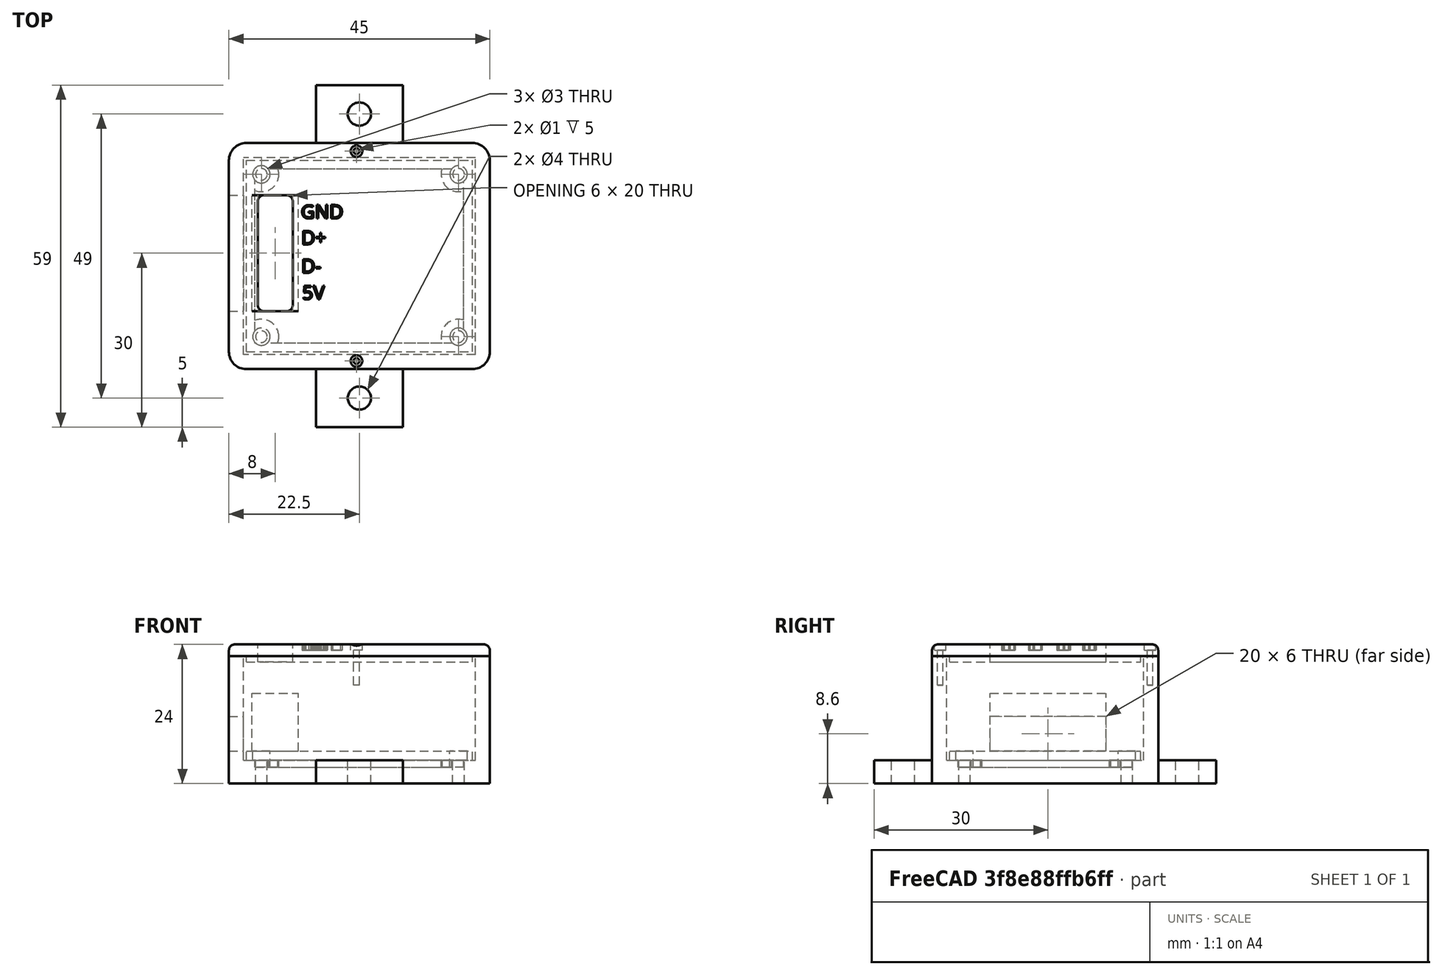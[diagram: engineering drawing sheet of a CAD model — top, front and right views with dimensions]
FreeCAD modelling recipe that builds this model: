
FCSTD DOCUMENT  (FreeCAD 0.17R13522 (Git))
Label: Caja Bridge TCP-RTU V2
License: All rights reserved
LicenseURL: http://en.wikipedia.org/wiki/All_rights_reserved
objects: Part::Cylinder×20, Part::Box×12, Part::MultiFuse×12, Part::Cut×11, Part::Fillet×4, Part::Part2DObjectPython×4, Part::Extrusion×4
note: 67 computed .brp shape members not serialized (recipe doc carries the construction recipe); baked Part::Feature solids carry a one-line shape summary decoded from their .brp

FEATURE [Part::Box] Box  label="Cubo"
  AttacherType = Attacher::AttachEngine3D
  Height = 1.6
  Length = 39
  Placement = pos=(0,12,0) rot=(0,0,1;0rad)
  Width = 33
FEATURE [Part::Cylinder] Cylinder  label="Cilindro"
  Angle = 360
  AttacherType = Attacher::AttachEngine3D
  Height = 10
  Placement = pos=(2.6,14.6,-5) rot=(0,0,1;0rad)
  Radius = 1.5
FEATURE [Part::Cylinder] Cylinder001  label="Cilindro001"
  Angle = 360
  AttacherType = Attacher::AttachEngine3D
  Height = 10
  Placement = pos=(36.6,14.6,-5) rot=(0,0,1;0rad)
  Radius = 1.5
FEATURE [Part::Cylinder] Cylinder002  label="Cilindro002"
  Angle = 360
  AttacherType = Attacher::AttachEngine3D
  Height = 10
  Placement = pos=(36.6,42.6,-5) rot=(0,0,1;0rad)
  Radius = 1.5
FEATURE [Part::Cylinder] Cylinder003  label="Cilindro003"
  Angle = 360
  AttacherType = Attacher::AttachEngine3D
  Height = 10
  Placement = pos=(2.6,42.6,-5) rot=(0,0,1;0rad)
  Radius = 1.5
FEATURE [Part::Box] Box001  label="Cubo001"
  AttacherType = Attacher::AttachEngine3D
  Height = 10
  Length = 8
  Placement = pos=(1,19,1.6) rot=(0,0,1;0rad)
  Width = 20
FEATURE [Part::Box] Box002  label="Cubo002"
  AttacherType = Attacher::AttachEngine3D
  Height = 20
  Length = 40
  Placement = pos=(-0.5,11.5,0) rot=(0,0,1;0rad)
  Width = 34
FEATURE [Part::Box] Box003  label="Cubo003"
  AttacherType = Attacher::AttachEngine3D
  Height = 22
  Length = 45
  Placement = pos=(-3,9,-4) rot=(0,0,1;0rad)
  Width = 39
FEATURE [Part::Box] Box004  label="Cubo004"
  AttacherType = Attacher::AttachEngine3D
  Height = 1.5
  Length = 36
  Placement = pos=(1.5,13.5,-1.2) rot=(0,0,1;0rad)
  Width = 30
FEATURE [Part::MultiFuse] Fusion
  Refine = true
  Shapes = -> [Box,Box004]
FEATURE [Part::MultiFuse] Fusion001
  Refine = true
  Shapes = -> [Fusion,Box001]
FEATURE [Part::MultiFuse] Fusion002
  Refine = true
  Shapes = -> [Cylinder,Cylinder003,Cylinder002,Cylinder001]
FEATURE [Part::Cut] Cut  label="Electronica V2"
  Base = -> Fusion001
  Refine = true
  Tool = -> Fusion002
FEATURE [Part::Box] Box005  label="Cubo005"
  AttacherType = Attacher::AttachEngine3D
  Height = 1.5
  Length = 36
  Placement = pos=(1.5,13.5,-1.2) rot=(0,0,1;0rad)
  Width = 30
FEATURE [Part::Box] Box006  label="Cubo006"
  AttacherType = Attacher::AttachEngine3D
  Height = 6
  Length = 22
  Placement = pos=(-10,19,1.6) rot=(0,0,1;0rad)
  Width = 20
FEATURE [Part::Box] Box007  label="Cubo007"
  AttacherType = Attacher::AttachEngine3D
  Height = 2
  Length = 45
  Placement = pos=(-3,9,18) rot=(0,0,1;0rad)
  Width = 39
FEATURE [Part::Box] Box008  label="Cubo008"
  AttacherType = Attacher::AttachEngine3D
  Height = 3
  Length = 39
  Placement = pos=(0,12,17) rot=(0,0,1;0rad)
  Width = 33
FEATURE [Part::Cylinder] Cylinder004  label="Cilindro004"
  Angle = 360
  AttacherType = Attacher::AttachEngine3D
  Height = 10
  Placement = pos=(2.6,14.6,-5) rot=(0,0,1;0rad)
  Radius = 1
FEATURE [Part::Cylinder] Cylinder005  label="Cilindro005"
  Angle = 360
  AttacherType = Attacher::AttachEngine3D
  Height = 10
  Placement = pos=(36.6,14.6,-5) rot=(0,0,1;0rad)
  Radius = 1
FEATURE [Part::Cylinder] Cylinder006  label="Cilindro006"
  Angle = 360
  AttacherType = Attacher::AttachEngine3D
  Height = 10
  Placement = pos=(36.6,42.6,-5) rot=(0,0,1;0rad)
  Radius = 1
FEATURE [Part::Cylinder] Cylinder007  label="Cilindro007"
  Angle = 360
  AttacherType = Attacher::AttachEngine3D
  Height = 10
  Placement = pos=(2.6,42.6,-5) rot=(0,0,1;0rad)
  Radius = 1
FEATURE [Part::Cylinder] Cylinder008  label="Cilindro008"
  Angle = 360
  AttacherType = Attacher::AttachEngine3D
  Height = 3
  Placement = pos=(2.6,42.6,-3) rot=(0,0,1;0rad)
  Radius = 3
FEATURE [Part::Cylinder] Cylinder009  label="Cilindro009"
  Angle = 360
  AttacherType = Attacher::AttachEngine3D
  Height = 3
  Placement = pos=(36.6,14.6,-3) rot=(0,0,1;0rad)
  Radius = 3
FEATURE [Part::Cylinder] Cylinder010  label="Cilindro010"
  Angle = 360
  AttacherType = Attacher::AttachEngine3D
  Height = 3
  Placement = pos=(2.6,14.6,-3) rot=(0,0,1;0rad)
  Radius = 3
FEATURE [Part::Cylinder] Cylinder011  label="Cilindro011"
  Angle = 360
  AttacherType = Attacher::AttachEngine3D
  Height = 3
  Placement = pos=(36.6,42.6,-3) rot=(0,0,1;0rad)
  Radius = 3
FEATURE [Part::MultiFuse] Fusion006
  Refine = true
  Shapes = -> [Cylinder007,Cylinder005,Cylinder004,Cylinder006]
FEATURE [Part::MultiFuse] Fusion007
  Refine = true
  Shapes = -> [Box007,Box008]
FEATURE [Part::Cylinder] Cylinder012  label="Cilindro012"
  Angle = 360
  AttacherType = Attacher::AttachEngine3D
  Height = 10
  Placement = pos=(19,10.4,13) rot=(0,0,1;0rad)
  Radius = 0.5
FEATURE [Part::Cylinder] Cylinder013  label="Cilindro013"
  Angle = 360
  AttacherType = Attacher::AttachEngine3D
  Height = 10
  Placement = pos=(19,46.6,13) rot=(0,0,1;0rad)
  Radius = 0.5
FEATURE [Part::MultiFuse] Fusion008
  Refine = true
  Shapes = -> [Cylinder012,Cylinder013]
FEATURE [Part::Cylinder] Cylinder014  label="Cilindro014"
  Angle = 360
  AttacherType = Attacher::AttachEngine3D
  Height = 10
  Placement = pos=(19,46.6,13) rot=(0,0,1;0rad)
  Radius = 0.5
FEATURE [Part::Cylinder] Cylinder015  label="Cilindro015"
  Angle = 360
  AttacherType = Attacher::AttachEngine3D
  Height = 10
  Placement = pos=(19,10.4,13) rot=(0,0,1;0rad)
  Radius = 0.5
FEATURE [Part::MultiFuse] Fusion009
  Refine = true
  Shapes = -> [Cylinder015,Cylinder014]
FEATURE [Part::Cylinder] Cylinder016  label="Cilindro016"
  Angle = 360
  AttacherType = Attacher::AttachEngine3D
  Height = 10
  Placement = pos=(19,10.4,19) rot=(0,0,1;0rad)
  Radius = 1
FEATURE [Part::Cylinder] Cylinder017  label="Cilindro017"
  Angle = 360
  AttacherType = Attacher::AttachEngine3D
  Height = 10
  Placement = pos=(19,46.6,19) rot=(0,0,1;0rad)
  Radius = 1
FEATURE [Part::MultiFuse] Fusion010
  Refine = true
  Shapes = -> [Cylinder016,Cylinder017]
FEATURE [Part::Box] Box009  label="Cubo009"
  AttacherType = Attacher::AttachEngine3D
  Height = 4
  Length = 15
  Placement = pos=(12,-13,-4) rot=(0,0,1;0rad)
  Width = 10
FEATURE [Part::Cylinder] Cylinder018  label="Cilindro018"
  Angle = 360
  AttacherType = Attacher::AttachEngine3D
  Height = 10
  Placement = pos=(19.5,-8,-7) rot=(0,0,1;0rad)
  Radius = 2
FEATURE [Part::Cut] Cut007
  Base = -> Box009
  Placement = pos=(0,12,0) rot=(0,0,1;0rad)
  Refine = true
  Tool = -> Cylinder018
FEATURE [Part::Cylinder] Cylinder019  label="Cilindro019"
  Angle = 360
  AttacherType = Attacher::AttachEngine3D
  Height = 10
  Placement = pos=(19.5,-8,-7) rot=(0,0,1;0rad)
  Radius = 2
FEATURE [Part::Box] Box010  label="Cubo010"
  AttacherType = Attacher::AttachEngine3D
  Height = 4
  Length = 15
  Placement = pos=(12,-13,-4) rot=(0,0,1;0rad)
  Width = 10
FEATURE [Part::Cut] Cut008
  Base = -> Box010
  Placement = pos=(0,61,0) rot=(0,0,1;0rad)
  Refine = true
  Tool = -> Cylinder019
FEATURE [Part::Fillet] Fillet
  Base = -> Fusion007
  Edges = 4 edges r=3: [Edge1,Edge3,Edge6,Edge9]
FEATURE [Part::Fillet] Fillet003
  Base = -> Fillet
  Edges = 4 edges r=1: [Edge1,Edge7,Edge8,Edge11]
FEATURE [Part::Cut] Cut009
  Base = -> Fillet003
  Refine = true
  Tool = -> Fusion010
FEATURE [Part::Cut] Cut010  label="Tapa V2"
  Base = -> Cut009
  Refine = true
  Tool = -> Fusion009
FEATURE [Part::Box] Box011  label="Cubo011"
  AttacherType = Attacher::AttachEngine3D
  Height = 48
  Length = 6
  Placement = pos=(2,19,1.6) rot=(0,0,1;0rad)
  Width = 20
FEATURE [Part::Cut] Cut011
  Base = -> Cut010
  Refine = true
  Tool = -> Box011
FEATURE [Part::Fillet] Fillet004  label="tapa V1"
  Base = -> Cut011
  Edges = 4 edges r=1: [Edge75,Edge76,Edge78,Edge80]
FEATURE [Part::Part2DObjectPython] ShapeString  label="GND"  # Draft 2D object (typed FeaturePython)
  FontFile = <path>
  Placement = pos=(9.41125,34.9742,20) rot=(0,0,1;0rad)
  Size = 3
  String = GND
  Support = -> [Fillet004]
  Tracking = 0
FEATURE [Part::Part2DObjectPython] ShapeString001  # Draft 2D object (typed FeaturePython)
  FontFile = C:/Program Files/FreeCAD 0.17/OpenSans-Regular.ttf
  Placement = pos=(9.47171,30.4997,20) rot=(0,0,1;0rad)
  Size = 3
  String = D+
  Tracking = 0
FEATURE [Part::Part2DObjectPython] ShapeString002  # Draft 2D object (typed FeaturePython)
  FontFile = C:/Program Files/FreeCAD 0.17/OpenSans-Regular.ttf
  Placement = pos=(9.47171,25.6019,20) rot=(0,0,1;0rad)
  Size = 3
  String = D-
  Tracking = 0
FEATURE [Part::Part2DObjectPython] ShapeString003  # Draft 2D object (typed FeaturePython)
  FontFile = C:/Program Files/FreeCAD 0.17/OpenSans-Regular.ttf
  Placement = pos=(9.65311,21.0064,20) rot=(0,0,1;0rad)
  Size = 3
  String = 5V
  Support = -> [Fillet004]
  Tracking = 0
FEATURE [Part::Extrusion] Extrude
  Base = -> ShapeString
  Dir = (0,0,-1)
  DirMode = 0
  FaceMakerClass = Part::FaceMakerBullseye
  LengthFwd = 1
  LengthRev = 0
  Solid = true
  Symmetric = false
FEATURE [Part::Extrusion] Extrude001
  Base = -> ShapeString001
  Dir = (0,0,-1)
  DirMode = 0
  FaceMakerClass = Part::FaceMakerBullseye
  LengthFwd = 1
  LengthRev = 0
  Solid = true
  Symmetric = false
FEATURE [Part::Extrusion] Extrude002
  Base = -> ShapeString002
  Dir = (0,0,-1)
  DirMode = 0
  FaceMakerClass = Part::FaceMakerBullseye
  LengthFwd = 1
  LengthRev = 0
  Solid = true
  Symmetric = false
FEATURE [Part::Extrusion] Extrude003
  Base = -> ShapeString003
  Dir = (0,0,-1)
  DirMode = 0
  FaceMakerClass = Part::FaceMakerBullseye
  LengthFwd = 1
  LengthRev = 0
  Solid = true
  Symmetric = false
FEATURE [Part::MultiFuse] Fusion012
  Refine = true
  Shapes = -> [Extrude003,Extrude,Extrude001,Extrude002]
FEATURE [Part::Cut] Cut012  label="tapa V2"
  Base = -> Fillet004
  Refine = true
  Tool = -> Fusion012
FEATURE [Part::MultiFuse] Fusion013
  Refine = true
  Shapes = -> [Box002,Box005]
FEATURE [Part::Cut] Cut013
  Base = -> Box003
  Refine = true
  Tool = -> Fusion013
FEATURE [Part::Cut] Cut014
  Base = -> Cut013
  Refine = true
  Tool = -> Box006
FEATURE [Part::MultiFuse] Fusion014
  Refine = true
  Shapes = -> [Cylinder008,Cylinder009,Cylinder010,Cylinder011,Cut014]
FEATURE [Part::Cut] Cut015
  Base = -> Fusion014
  Refine = true
  Tool = -> Fusion006
FEATURE [Part::Cut] Cut016
  Base = -> Cut015
  Refine = true
  Tool = -> Fusion008
FEATURE [Part::MultiFuse] Fusion015
  Refine = true
  Shapes = -> [Cut016,Cut007,Cut008]
FEATURE [Part::Fillet] Fillet005  label="Caja V2"
  Base = -> Fusion015
  Edges = 4 edges r=3: [Edge1,Edge4,Edge14,Edge29]
note: 1 file-system path scrubbed to <path> (originals preserved in the JSON sidecar)
